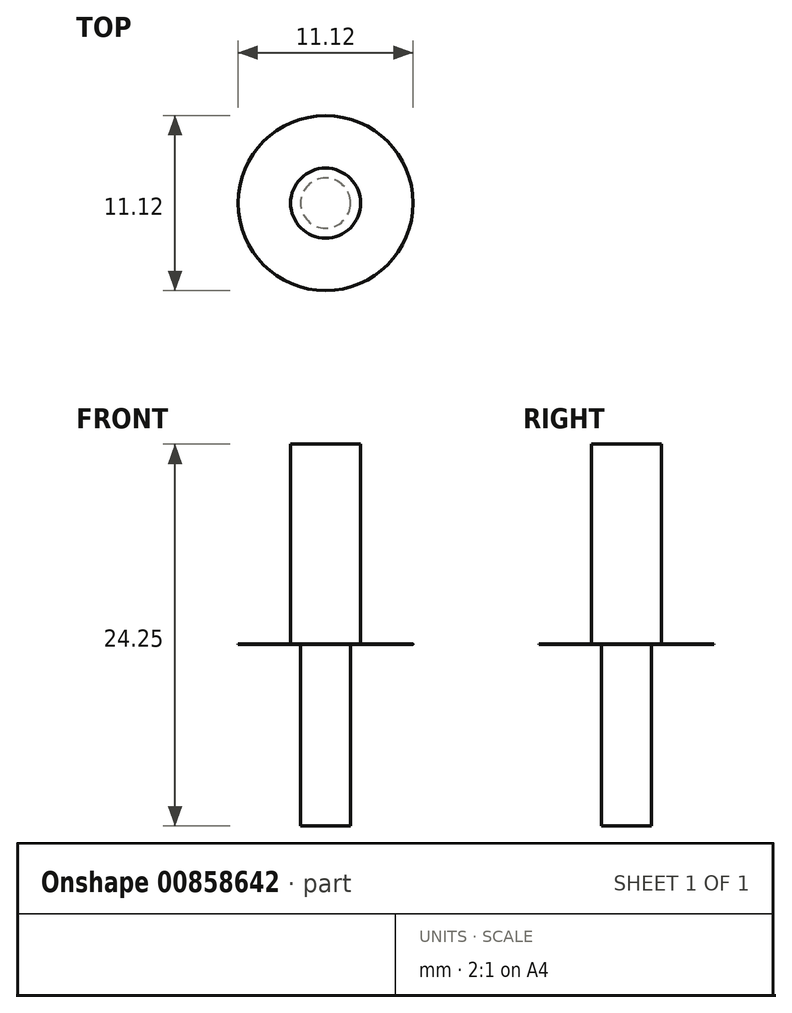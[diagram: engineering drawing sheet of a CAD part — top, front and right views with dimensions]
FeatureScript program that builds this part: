
annotation { "Feature Type Name" : "Feature", "Feature Type Description" : "" }
export const myFeature = defineFeature(function(context is Context, id is Id, definition is map)
    precondition{}
    {
        {
            var Q0;
            Q0=qCreatedBy(makeId("Top.planeOp"),FACE);
            var sketch = newSketch(context, id + "F0", { "sketchPlane" : qUnion([Q0])});
            skCircle(sketch, "E0", {"center": v(0, 0) * mm, "radius": 5.56 * mm});
            skSolve(sketch);
        }
        {
            var Q0;
            Q0 = qSketchRegion(id + "F0", true);
            extrude(context, id + "F1", {"entities" : qUnion([Q0]), "depth" : 3 / 406.4 * mm, "offsetDistance" : 25 * mm});
        }
        {
            var Q0;
            Q0=makeQuery(id+"F1.opExtrude","CAP_FACE",FACE,{"disambiguationData":[OSD([sQuery(id+"F0.wireOp",EDGE,"E0")])],"isStart":false});
            var sketch = newSketch(context, id + "F2", { "sketchPlane" : qUnion([Q0])});
            skCircle(sketch, "E1", {"center": v(0, 0) * mm, "radius": 2.22 * mm});
            skSolve(sketch);
        }
        {
            var Q0;
            Q0 = qSketchRegion(id + "F2", true);
            extrude(context, id + "F3", {"entities" : qUnion([Q0]), "operationType" : NewBodyOperationType.ADD, "depth" : 12.7 * mm, "offsetDistance" : 25 * mm});
        }
        {
            var Q0;
            Q0=makeQuery(id+"F1.opExtrude","CAP_FACE",FACE,{"disambiguationData":[OSD([sQuery(id+"F0.wireOp",EDGE,"E0")])],"isStart":true});
            var sketch = newSketch(context, id + "F4", { "sketchPlane" : qUnion([Q0])});
            skCircle(sketch, "E2", {"center": v(0, 0) * mm, "radius": 1.59 * mm});
            skSolve(sketch);
        }
        {
            var Q0;
            Q0 = qSketchRegion(id + "F4", true);
            extrude(context, id + "F5", {"entities" : qUnion([Q0]), "operationType" : NewBodyOperationType.ADD, "depth" : 11.54 * mm, "offsetDistance" : 25 * mm});
        }
    });
